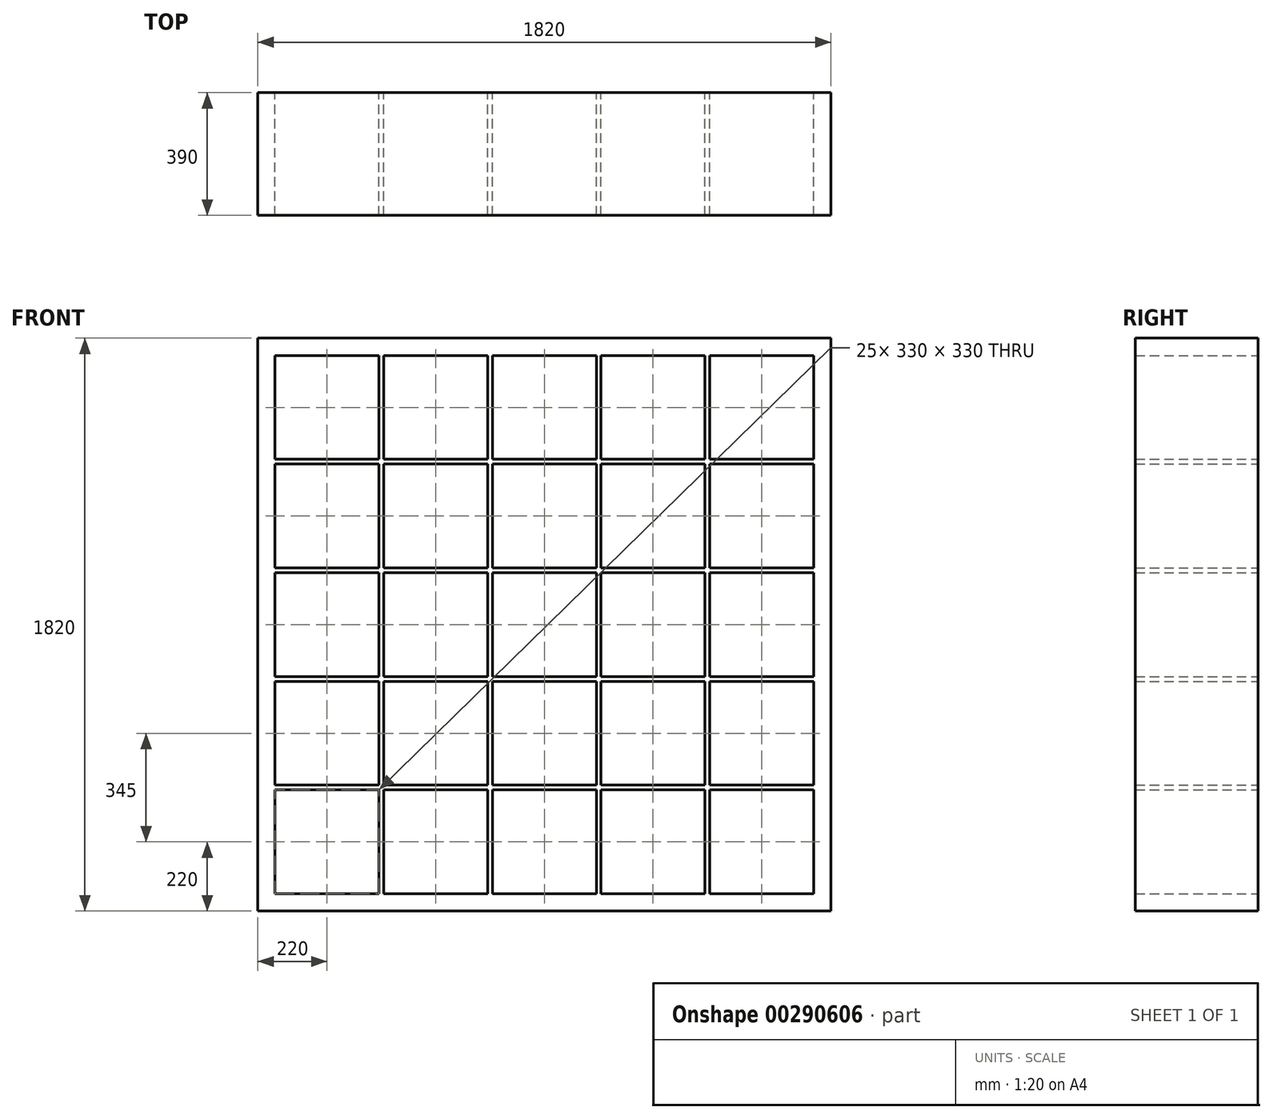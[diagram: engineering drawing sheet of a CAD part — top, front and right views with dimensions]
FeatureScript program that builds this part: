
annotation { "Feature Type Name" : "Feature", "Feature Type Description" : "" }
export const myFeature = defineFeature(function(context is Context, id is Id, definition is map)
    precondition{}
    {
        {
            var Q0;
            Q0=qCreatedBy(makeId("Front.planeOp"),FACE);
            var sketch = newSketch(context, id + "F0", { "sketchPlane" : qUnion([Q0])});
            skLineSegment(sketch, "E0.bottom", {"start": v(0, 1820) * mm, "end": v(1820, 1820) * mm});
            skLineSegment(sketch, "E0.top", {"start": v(0, 0) * mm, "end": v(1820, 0) * mm});
            skLineSegment(sketch, "E0.left", {"start": v(0, 1820) * mm, "end": v(0, 0) * mm});
            skLineSegment(sketch, "E0.right", {"start": v(1820, 1820) * mm, "end": v(1820, 0) * mm});
            skSolve(sketch);
        }
        {
            var Q0;
            Q0=makeQuery(id+"F0.imprint","IMPRINT",FACE,{"disambiguationData":[TD([[makeQuery(id+"F0.imprint","IMPRINT",EDGE,{"derivedFrom":sQuery(id+"F0.wireOp",EDGE,"E0.bottom")}),-1.0]])]});
            extrude(context, id + "F1", {"entities" : qUnion([Q0]), "depth" : 390 * mm});
        }
        {
            var Q0;
            Q0=qCreatedBy(makeId("Front.planeOp"),FACE);
            var sketch = newSketch(context, id + "F2", { "sketchPlane" : qUnion([Q0])});
            skLineSegment(sketch, "E1.bottom", {"start": v(385, 385) * mm, "end": v(55, 385) * mm});
            skLineSegment(sketch, "E1.top", {"start": v(385, 55) * mm, "end": v(55, 55) * mm});
            skLineSegment(sketch, "E1.left", {"start": v(385, 385) * mm, "end": v(385, 55) * mm});
            skLineSegment(sketch, "E1.right", {"start": v(55, 385) * mm, "end": v(55, 55) * mm});
            skLineSegment(sketch, "E2.0.1.0", {"start": v(385, 730) * mm, "end": v(385, 400) * mm});
            skLineSegment(sketch, "E2.0.1.1", {"start": v(385, 400) * mm, "end": v(55, 400) * mm});
            skLineSegment(sketch, "E2.0.1.2", {"start": v(55, 730) * mm, "end": v(55, 400) * mm});
            skLineSegment(sketch, "E2.0.1.3", {"start": v(385, 730) * mm, "end": v(55, 730) * mm});
            skLineSegment(sketch, "E2.0.2.0", {"start": v(385, 1075) * mm, "end": v(385, 745) * mm});
            skLineSegment(sketch, "E2.0.2.1", {"start": v(385, 745) * mm, "end": v(55, 745) * mm});
            skLineSegment(sketch, "E2.0.2.2", {"start": v(55, 1075) * mm, "end": v(55, 745) * mm});
            skLineSegment(sketch, "E2.0.2.3", {"start": v(385, 1075) * mm, "end": v(55, 1075) * mm});
            skLineSegment(sketch, "E2.0.3.0", {"start": v(385, 1420) * mm, "end": v(385, 1090) * mm});
            skLineSegment(sketch, "E2.0.3.1", {"start": v(385, 1090) * mm, "end": v(55, 1090) * mm});
            skLineSegment(sketch, "E2.0.3.2", {"start": v(55, 1420) * mm, "end": v(55, 1090) * mm});
            skLineSegment(sketch, "E2.0.3.3", {"start": v(385, 1420) * mm, "end": v(55, 1420) * mm});
            skLineSegment(sketch, "E2.0.4.0", {"start": v(385, 1765) * mm, "end": v(385, 1435) * mm});
            skLineSegment(sketch, "E2.0.4.1", {"start": v(385, 1435) * mm, "end": v(55, 1435) * mm});
            skLineSegment(sketch, "E2.0.4.2", {"start": v(55, 1765) * mm, "end": v(55, 1435) * mm});
            skLineSegment(sketch, "E2.0.4.3", {"start": v(385, 1765) * mm, "end": v(55, 1765) * mm});
            skLineSegment(sketch, "E2.1.0.0", {"start": v(730, 385) * mm, "end": v(730, 55) * mm});
            skLineSegment(sketch, "E2.1.0.1", {"start": v(730, 55) * mm, "end": v(400, 55) * mm});
            skLineSegment(sketch, "E2.1.0.2", {"start": v(400, 385) * mm, "end": v(400, 55) * mm});
            skLineSegment(sketch, "E2.1.0.3", {"start": v(730, 385) * mm, "end": v(400, 385) * mm});
            skLineSegment(sketch, "E2.1.1.0", {"start": v(730, 730) * mm, "end": v(730, 400) * mm});
            skLineSegment(sketch, "E2.1.1.1", {"start": v(730, 400) * mm, "end": v(400, 400) * mm});
            skLineSegment(sketch, "E2.1.1.2", {"start": v(400, 730) * mm, "end": v(400, 400) * mm});
            skLineSegment(sketch, "E2.1.1.3", {"start": v(730, 730) * mm, "end": v(400, 730) * mm});
            skLineSegment(sketch, "E2.1.2.0", {"start": v(730, 1075) * mm, "end": v(730, 745) * mm});
            skLineSegment(sketch, "E2.1.2.1", {"start": v(730, 745) * mm, "end": v(400, 745) * mm});
            skLineSegment(sketch, "E2.1.2.2", {"start": v(400, 1075) * mm, "end": v(400, 745) * mm});
            skLineSegment(sketch, "E2.1.2.3", {"start": v(730, 1075) * mm, "end": v(400, 1075) * mm});
            skLineSegment(sketch, "E2.1.3.0", {"start": v(730, 1420) * mm, "end": v(730, 1090) * mm});
            skLineSegment(sketch, "E2.1.3.1", {"start": v(730, 1090) * mm, "end": v(400, 1090) * mm});
            skLineSegment(sketch, "E2.1.3.2", {"start": v(400, 1420) * mm, "end": v(400, 1090) * mm});
            skLineSegment(sketch, "E2.1.3.3", {"start": v(730, 1420) * mm, "end": v(400, 1420) * mm});
            skLineSegment(sketch, "E2.1.4.0", {"start": v(730, 1765) * mm, "end": v(730, 1435) * mm});
            skLineSegment(sketch, "E2.1.4.1", {"start": v(730, 1435) * mm, "end": v(400, 1435) * mm});
            skLineSegment(sketch, "E2.1.4.2", {"start": v(400, 1765) * mm, "end": v(400, 1435) * mm});
            skLineSegment(sketch, "E2.1.4.3", {"start": v(730, 1765) * mm, "end": v(400, 1765) * mm});
            skLineSegment(sketch, "E2.2.0.0", {"start": v(1075, 385) * mm, "end": v(1075, 55) * mm});
            skLineSegment(sketch, "E2.2.0.1", {"start": v(1075, 55) * mm, "end": v(745, 55) * mm});
            skLineSegment(sketch, "E2.2.0.2", {"start": v(745, 385) * mm, "end": v(745, 55) * mm});
            skLineSegment(sketch, "E2.2.0.3", {"start": v(1075, 385) * mm, "end": v(745, 385) * mm});
            skLineSegment(sketch, "E2.2.1.0", {"start": v(1075, 730) * mm, "end": v(1075, 400) * mm});
            skLineSegment(sketch, "E2.2.1.1", {"start": v(1075, 400) * mm, "end": v(745, 400) * mm});
            skLineSegment(sketch, "E2.2.1.2", {"start": v(745, 730) * mm, "end": v(745, 400) * mm});
            skLineSegment(sketch, "E2.2.1.3", {"start": v(1075, 730) * mm, "end": v(745, 730) * mm});
            skLineSegment(sketch, "E2.2.2.0", {"start": v(1075, 1075) * mm, "end": v(1075, 745) * mm});
            skLineSegment(sketch, "E2.2.2.1", {"start": v(1075, 745) * mm, "end": v(745, 745) * mm});
            skLineSegment(sketch, "E2.2.2.2", {"start": v(745, 1075) * mm, "end": v(745, 745) * mm});
            skLineSegment(sketch, "E2.2.2.3", {"start": v(1075, 1075) * mm, "end": v(745, 1075) * mm});
            skLineSegment(sketch, "E2.2.3.0", {"start": v(1075, 1420) * mm, "end": v(1075, 1090) * mm});
            skLineSegment(sketch, "E2.2.3.1", {"start": v(1075, 1090) * mm, "end": v(745, 1090) * mm});
            skLineSegment(sketch, "E2.2.3.2", {"start": v(745, 1420) * mm, "end": v(745, 1090) * mm});
            skLineSegment(sketch, "E2.2.3.3", {"start": v(1075, 1420) * mm, "end": v(745, 1420) * mm});
            skLineSegment(sketch, "E2.2.4.0", {"start": v(1075, 1765) * mm, "end": v(1075, 1435) * mm});
            skLineSegment(sketch, "E2.2.4.1", {"start": v(1075, 1435) * mm, "end": v(745, 1435) * mm});
            skLineSegment(sketch, "E2.2.4.2", {"start": v(745, 1765) * mm, "end": v(745, 1435) * mm});
            skLineSegment(sketch, "E2.2.4.3", {"start": v(1075, 1765) * mm, "end": v(745, 1765) * mm});
            skLineSegment(sketch, "E2.3.0.0", {"start": v(1420, 385) * mm, "end": v(1420, 55) * mm});
            skLineSegment(sketch, "E2.3.0.1", {"start": v(1420, 55) * mm, "end": v(1090, 55) * mm});
            skLineSegment(sketch, "E2.3.0.2", {"start": v(1090, 385) * mm, "end": v(1090, 55) * mm});
            skLineSegment(sketch, "E2.3.0.3", {"start": v(1420, 385) * mm, "end": v(1090, 385) * mm});
            skLineSegment(sketch, "E2.3.1.0", {"start": v(1420, 730) * mm, "end": v(1420, 400) * mm});
            skLineSegment(sketch, "E2.3.1.1", {"start": v(1420, 400) * mm, "end": v(1090, 400) * mm});
            skLineSegment(sketch, "E2.3.1.2", {"start": v(1090, 730) * mm, "end": v(1090, 400) * mm});
            skLineSegment(sketch, "E2.3.1.3", {"start": v(1420, 730) * mm, "end": v(1090, 730) * mm});
            skLineSegment(sketch, "E2.3.2.0", {"start": v(1420, 1075) * mm, "end": v(1420, 745) * mm});
            skLineSegment(sketch, "E2.3.2.1", {"start": v(1420, 745) * mm, "end": v(1090, 745) * mm});
            skLineSegment(sketch, "E2.3.2.2", {"start": v(1090, 1075) * mm, "end": v(1090, 745) * mm});
            skLineSegment(sketch, "E2.3.2.3", {"start": v(1420, 1075) * mm, "end": v(1090, 1075) * mm});
            skLineSegment(sketch, "E2.3.3.0", {"start": v(1420, 1420) * mm, "end": v(1420, 1090) * mm});
            skLineSegment(sketch, "E2.3.3.1", {"start": v(1420, 1090) * mm, "end": v(1090, 1090) * mm});
            skLineSegment(sketch, "E2.3.3.2", {"start": v(1090, 1420) * mm, "end": v(1090, 1090) * mm});
            skLineSegment(sketch, "E2.3.3.3", {"start": v(1420, 1420) * mm, "end": v(1090, 1420) * mm});
            skLineSegment(sketch, "E2.3.4.0", {"start": v(1420, 1765) * mm, "end": v(1420, 1435) * mm});
            skLineSegment(sketch, "E2.3.4.1", {"start": v(1420, 1435) * mm, "end": v(1090, 1435) * mm});
            skLineSegment(sketch, "E2.3.4.2", {"start": v(1090, 1765) * mm, "end": v(1090, 1435) * mm});
            skLineSegment(sketch, "E2.3.4.3", {"start": v(1420, 1765) * mm, "end": v(1090, 1765) * mm});
            skLineSegment(sketch, "E2.4.0.0", {"start": v(1765, 385) * mm, "end": v(1765, 55) * mm});
            skLineSegment(sketch, "E2.4.0.1", {"start": v(1765, 55) * mm, "end": v(1435, 55) * mm});
            skLineSegment(sketch, "E2.4.0.2", {"start": v(1435, 385) * mm, "end": v(1435, 55) * mm});
            skLineSegment(sketch, "E2.4.0.3", {"start": v(1765, 385) * mm, "end": v(1435, 385) * mm});
            skLineSegment(sketch, "E2.4.1.0", {"start": v(1765, 730) * mm, "end": v(1765, 400) * mm});
            skLineSegment(sketch, "E2.4.1.1", {"start": v(1765, 400) * mm, "end": v(1435, 400) * mm});
            skLineSegment(sketch, "E2.4.1.2", {"start": v(1435, 730) * mm, "end": v(1435, 400) * mm});
            skLineSegment(sketch, "E2.4.1.3", {"start": v(1765, 730) * mm, "end": v(1435, 730) * mm});
            skLineSegment(sketch, "E2.4.2.0", {"start": v(1765, 1075) * mm, "end": v(1765, 745) * mm});
            skLineSegment(sketch, "E2.4.2.1", {"start": v(1765, 745) * mm, "end": v(1435, 745) * mm});
            skLineSegment(sketch, "E2.4.2.2", {"start": v(1435, 1075) * mm, "end": v(1435, 745) * mm});
            skLineSegment(sketch, "E2.4.2.3", {"start": v(1765, 1075) * mm, "end": v(1435, 1075) * mm});
            skLineSegment(sketch, "E2.4.3.0", {"start": v(1765, 1420) * mm, "end": v(1765, 1090) * mm});
            skLineSegment(sketch, "E2.4.3.1", {"start": v(1765, 1090) * mm, "end": v(1435, 1090) * mm});
            skLineSegment(sketch, "E2.4.3.2", {"start": v(1435, 1420) * mm, "end": v(1435, 1090) * mm});
            skLineSegment(sketch, "E2.4.3.3", {"start": v(1765, 1420) * mm, "end": v(1435, 1420) * mm});
            skLineSegment(sketch, "E2.4.4.0", {"start": v(1765, 1765) * mm, "end": v(1765, 1435) * mm});
            skLineSegment(sketch, "E2.4.4.1", {"start": v(1765, 1435) * mm, "end": v(1435, 1435) * mm});
            skLineSegment(sketch, "E2.4.4.2", {"start": v(1435, 1765) * mm, "end": v(1435, 1435) * mm});
            skLineSegment(sketch, "E2.4.4.3", {"start": v(1765, 1765) * mm, "end": v(1435, 1765) * mm});
            skLineSegment(sketch, "E2.direction1", {"start": v(385, 55) * mm, "end": v(730, 55) * mm, "construction": true});
            skLineSegment(sketch, "E2.direction2", {"start": v(385, 55) * mm, "end": v(385, 400) * mm, "construction": true});
            skSolve(sketch);
        }
        {
            var Q0;
            Q0 = qSketchRegion(id + "F2", true);
            extrude(context, id + "F3", {"entities" : qUnion([Q0]), "operationType" : NewBodyOperationType.REMOVE, "depth" : 740.6 * mm});
        }
    });
